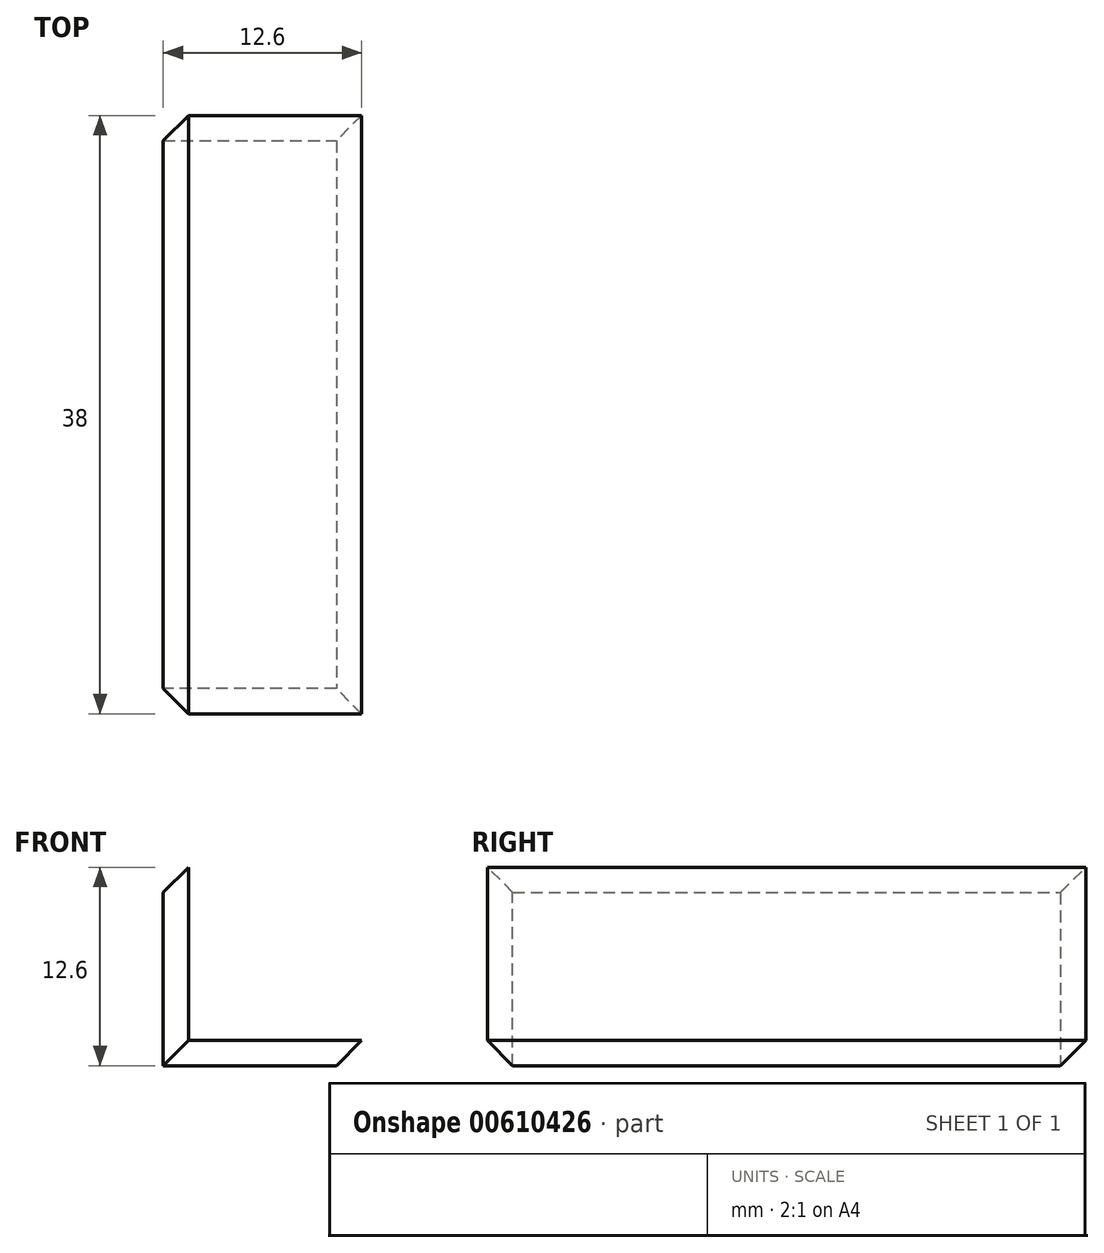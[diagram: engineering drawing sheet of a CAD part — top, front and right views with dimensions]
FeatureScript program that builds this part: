
annotation { "Feature Type Name" : "Feature", "Feature Type Description" : "" }
export const myFeature = defineFeature(function(context is Context, id is Id, definition is map)
    precondition{}
    {
        {
            var Q0;
            Q0=qCreatedBy(makeId("Front.planeOp"),FACE);
            var sketch = newSketch(context, id + "F0", { "sketchPlane" : qUnion([Q0])});
            skLineSegment(sketch, "E0", {"start": v(0, 0) * mm, "end": v(12.6, 0) * mm});
            skLineSegment(sketch, "E1", {"start": v(12.6, 0) * mm, "end": v(12.6, 1.6) * mm});
            skLineSegment(sketch, "E2", {"start": v(12.6, 1.6) * mm, "end": v(1.6, 1.6) * mm});
            skLineSegment(sketch, "E3", {"start": v(1.6, 1.6) * mm, "end": v(1.6, 12.6) * mm});
            skLineSegment(sketch, "E4", {"start": v(1.6, 12.6) * mm, "end": v(0, 12.6) * mm});
            skLineSegment(sketch, "E5", {"start": v(0, 12.6) * mm, "end": v(0, 0) * mm});
            skSolve(sketch);
        }
        {
            var Q0;
            Q0 = qSketchRegion(id + "F0", true);
            extrude(context, id + "F1", {"entities" : qUnion([Q0]), "depth" : 38 * mm, "offsetDistance" : 25 * mm});
        }
        {
            var Q0;
            Q0=makeQuery(id+"F1.opExtrude","SWEPT_EDGE",EDGE,{"disambiguationData":[OSD([sQuery(id+"F0.wireOp",EDGE,"E0"),sQuery(id+"F0.wireOp",EDGE,"E1")])]});
            var Q1;
            Q1=makeQuery(id+"F1.opExtrude","SWEPT_EDGE",EDGE,{"disambiguationData":[OSD([sQuery(id+"F0.wireOp",EDGE,"E4"),sQuery(id+"F0.wireOp",EDGE,"E5")])]});
            var Q2;
            Q2=makeQuery(id+"F1.opExtrude","CAP_EDGE",EDGE,{"disambiguationData":[OSD([sQuery(id+"F0.wireOp",EDGE,"E5")])],"isStart":true});
            var Q3;
            Q3=makeQuery(id+"F1.opExtrude","CAP_EDGE",EDGE,{"disambiguationData":[OSD([sQuery(id+"F0.wireOp",EDGE,"E0")])],"isStart":true});
            var Q4;
            Q4=makeQuery(id+"F1.opExtrude","CAP_EDGE",EDGE,{"disambiguationData":[OSD([sQuery(id+"F0.wireOp",EDGE,"E5")])],"isStart":false});
            var Q5;
            Q5=makeQuery(id+"F1.opExtrude","CAP_EDGE",EDGE,{"disambiguationData":[OSD([sQuery(id+"F0.wireOp",EDGE,"E0")])],"isStart":false});
            chamfer(context, id + "F2", {"entities" : qUnion([Q0, Q1, Q2, Q3, Q4, Q5]), "width" : 1.6 * mm, "tangentPropagation" : true});
        }
    });
